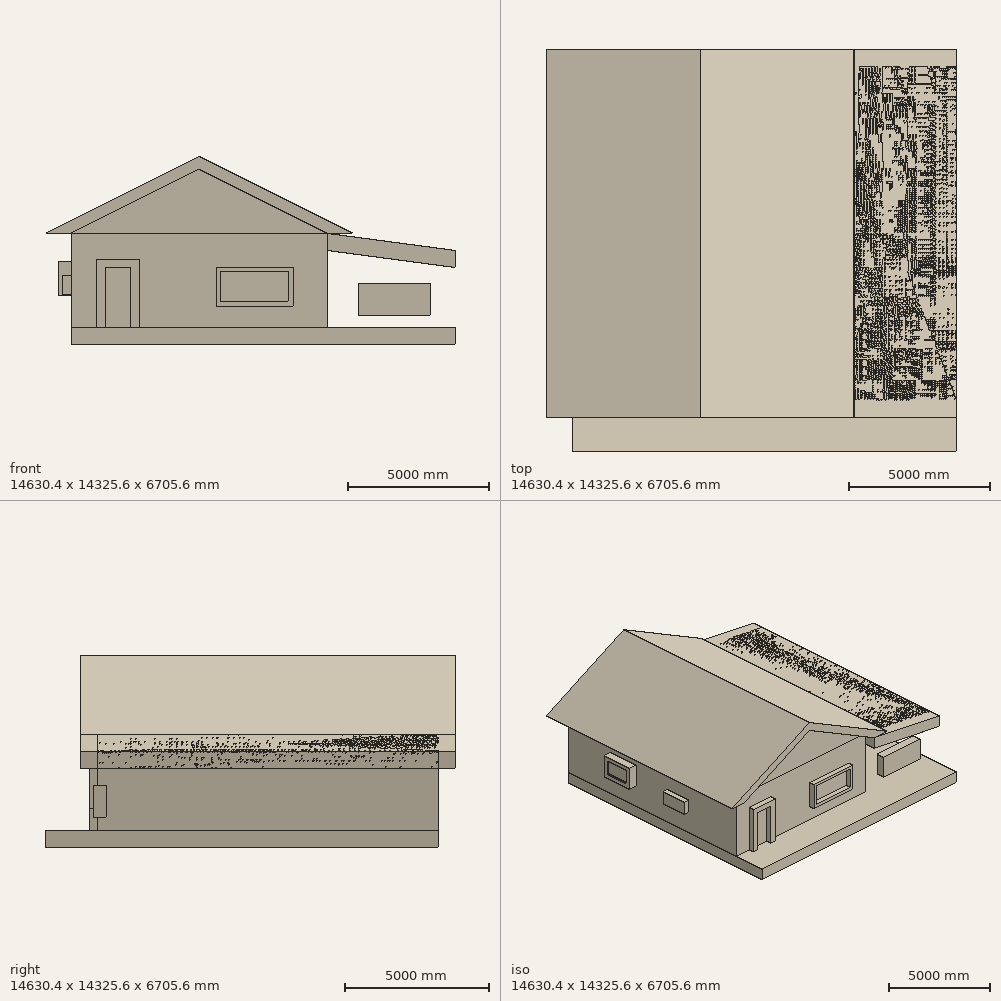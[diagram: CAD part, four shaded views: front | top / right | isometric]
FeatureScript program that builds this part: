
annotation { "Feature Type Name" : "Feature", "Feature Type Description" : "" }
export const myFeature = defineFeature(function(context is Context, id is Id, definition is map)
    precondition{}
    {
        {
            var Q0;
            Q0=qCreatedBy(makeId("Front.planeOp"),FACE);
            var sketch = newSketch(context, id + "F0", { "sketchPlane" : qUnion([Q0])});
            skLineSegment(sketch, "E0", {"start": v(0, 0) * mm, "end": v(-4572, 0) * mm});
            skLineSegment(sketch, "E1", {"start": v(0, 0) * mm, "end": v(4572, 0) * mm});
            skLineSegment(sketch, "E2", {"start": v(0, 0) * mm, "end": v(0, 2286) * mm});
            skLineSegment(sketch, "E3", {"start": v(-4572, 0) * mm, "end": v(-5486.4, 0) * mm});
            skLineSegment(sketch, "E4", {"start": v(4572, 0) * mm, "end": v(5486.4, 0) * mm});
            skLineSegment(sketch, "E5", {"start": v(0, 2286) * mm, "end": v(0, 2743.2) * mm});
            skLineSegment(sketch, "E6", {"start": v(-4572, 0) * mm, "end": v(0, 2286) * mm});
            skLineSegment(sketch, "E7", {"start": v(4572, 0) * mm, "end": v(0, 2286) * mm});
            skLineSegment(sketch, "E8", {"start": v(0, 2743.2) * mm, "end": v(5486.4, 0) * mm});
            skLineSegment(sketch, "E9", {"start": v(0, 2743.2) * mm, "end": v(-5486.4, 0) * mm});
            skLineSegment(sketch, "E10", {"start": v(-4572, 0) * mm, "end": v(-4572, -3352.8) * mm});
            skLineSegment(sketch, "E11", {"start": v(4572, 0) * mm, "end": v(4572, -3352.8) * mm});
            skLineSegment(sketch, "E12", {"start": v(4572, -3352.8) * mm, "end": v(4572, -3962.4) * mm});
            skLineSegment(sketch, "E13", {"start": v(-4572, -3352.8) * mm, "end": v(-4572, -3962.4) * mm});
            skLineSegment(sketch, "E14", {"start": v(-4572, -3352.8) * mm, "end": v(4572, -3352.8) * mm});
            skLineSegment(sketch, "E15", {"start": v(-4572, -3962.4) * mm, "end": v(4572, -3962.4) * mm});
            skLineSegment(sketch, "E16", {"start": v(4572, -3962.4) * mm, "end": v(9144, -3962.4) * mm});
            skLineSegment(sketch, "E17", {"start": v(4572, -3352.8) * mm, "end": v(9144, -3352.8) * mm});
            skLineSegment(sketch, "E18", {"start": v(9144, -3352.8) * mm, "end": v(9144, -3962.4) * mm});
            skLineSegment(sketch, "E19", {"start": v(9144, -3352.8) * mm, "end": v(9144, -609.6) * mm});
            skLineSegment(sketch, "E20", {"start": v(9144, -609.6) * mm, "end": v(4572, 0) * mm});
            skLineSegment(sketch, "E21", {"start": v(4572, 0) * mm, "end": v(4572, -609.6) * mm});
            skLineSegment(sketch, "E22", {"start": v(9144, -609.6) * mm, "end": v(9144, -1219.2) * mm});
            skLineSegment(sketch, "E23", {"start": v(4572, -609.6) * mm, "end": v(9144, -1219.2) * mm});
            skLineSegment(sketch, "E24", {"start": v(-3352.8, -3352.8) * mm, "end": v(-3352.8, -1219.2) * mm});
            skLineSegment(sketch, "E25", {"start": v(-3352.8, -1219.2) * mm, "end": v(-2438.4, -1219.2) * mm});
            skLineSegment(sketch, "E26", {"start": v(-2438.4, -3352.8) * mm, "end": v(-2438.4, -1219.2) * mm});
            skLineSegment(sketch, "E27.0", {"start": v(-3657.6, -3352.8) * mm, "end": v(-3657.6, -914.4) * mm});
            skLineSegment(sketch, "E27.1", {"start": v(-3657.6, -914.4) * mm, "end": v(-2133.6, -914.4) * mm});
            skLineSegment(sketch, "E27.2", {"start": v(-2133.6, -3352.8) * mm, "end": v(-2133.6, -914.4) * mm});
            skLineSegment(sketch, "E28.bottom", {"start": v(3352.8, -1219.2) * mm, "end": v(609.6, -1219.2) * mm});
            skLineSegment(sketch, "E28.top", {"start": v(609.6, -2590.8) * mm, "end": v(3352.8, -2590.8) * mm});
            skLineSegment(sketch, "E28.left", {"start": v(609.6, -2590.8) * mm, "end": v(609.6, -1219.2) * mm});
            skLineSegment(sketch, "E28.right", {"start": v(3352.8, -2590.8) * mm, "end": v(3352.8, -1219.2) * mm});
            skLineSegment(sketch, "E29.0", {"start": v(3200.4, -1371.6) * mm, "end": v(762, -1371.6) * mm});
            skLineSegment(sketch, "E29.1", {"start": v(3200.4, -2438.4) * mm, "end": v(3200.4, -1371.6) * mm});
            skLineSegment(sketch, "E29.2", {"start": v(762, -2438.4) * mm, "end": v(3200.4, -2438.4) * mm});
            skLineSegment(sketch, "E29.3", {"start": v(762, -2438.4) * mm, "end": v(762, -1371.6) * mm});
            skLineSegment(sketch, "E30.bottom", {"start": v(5683.3, -1784.2) * mm, "end": v(8242.86, -1784.2) * mm});
            skLineSegment(sketch, "E30.top", {"start": v(5683.3, -2924.87) * mm, "end": v(8242.86, -2924.87) * mm});
            skLineSegment(sketch, "E30.left", {"start": v(5683.3, -1784.2) * mm, "end": v(5683.3, -2924.87) * mm});
            skLineSegment(sketch, "E30.right", {"start": v(8242.86, -1784.2) * mm, "end": v(8242.86, -2924.87) * mm});
            skLineSegment(sketch, "E31.bottom", {"start": v(6044.98, -2173.7) * mm, "end": v(7909, -2173.7) * mm});
            skLineSegment(sketch, "E31.top", {"start": v(6044.98, -2591.02) * mm, "end": v(7909, -2591.02) * mm});
            skLineSegment(sketch, "E31.left", {"start": v(6044.98, -2173.7) * mm, "end": v(6044.98, -2591.02) * mm});
            skLineSegment(sketch, "E31.right", {"start": v(7909, -2173.7) * mm, "end": v(7909, -2591.02) * mm});
            skSolve(sketch);
        }
        {
            var Q0;
            Q0=makeQuery(id+"F0.imprint","IMPRINT",FACE,{"disambiguationData":[TD([[makeQuery(id+"F0.imprint","IMPRINT",EDGE,{"derivedFrom":sQuery(id+"F0.wireOp",EDGE,"E3")}),-1.0]])]});
            var Q1;
            Q1=makeQuery(id+"F0.imprint","IMPRINT",FACE,{"disambiguationData":[TD([[makeQuery(id+"F0.imprint","IMPRINT",EDGE,{"derivedFrom":sQuery(id+"F0.wireOp",EDGE,"E4")}),1.0]])]});
            var Q2;
            Q2=makeQuery(id+"F0.imprint","IMPRINT",FACE,{"disambiguationData":[TD([[makeQuery(id+"F0.imprint","IMPRINT",EDGE,{"derivedFrom":sQuery(id+"F0.wireOp",EDGE,"E20")}),1.0]])]});
            extrude(context, id + "F1", {"entities" : qUnion([Q0, Q1, Q2]), "depth" : 914.4 * mm, "offsetDistance" : 30.48 * mm, "hasSecondDirection" : true, "secondDirectionOppositeDirection" : true, "secondDirectionDepth" : 12192 * mm});
        }
        {
            var Q0;
            Q0=makeQuery(id+"F0.imprint","IMPRINT",FACE,{"disambiguationData":[TD([[makeQuery(id+"F0.imprint","IMPRINT",EDGE,{"derivedFrom":sQuery(id+"F0.wireOp",EDGE,"E0")}),-1.0]])]});
            var Q1;
            Q1=makeQuery(id+"F0.imprint","IMPRINT",FACE,{"disambiguationData":[TD([[makeQuery(id+"F0.imprint","IMPRINT",EDGE,{"derivedFrom":sQuery(id+"F0.wireOp",EDGE,"E1")}),1.0]])]});
            extrude(context, id + "F2", {"entities" : qUnion([Q0, Q1]), "operationType" : NewBodyOperationType.ADD, "depth" : 304.8 * mm, "offsetDistance" : 30.48 * mm, "hasSecondDirection" : true, "secondDirectionOppositeDirection" : true, "secondDirectionDepth" : 11582.4 * mm});
        }
        {
            var Q0;
            {var subQ4=sQuery(id+"F0.wireOp",EDGE,"E12");Q0=makeQuery(id+"F0.imprint","IMPRINT",FACE,{"disambiguationData":[TD([[makeQuery(id+"F0.imprint","IMPRINT",EDGE,{"derivedFrom":subQ4}),-1.0]])]});}
            var Q1;
            Q1=makeQuery(id+"F0.imprint","IMPRINT",FACE,{"disambiguationData":[TD([[makeQuery(id+"F0.imprint","IMPRINT",EDGE,{"derivedFrom":sQuery(id+"F0.wireOp",EDGE,"E12")}),1.0]])]});
            extrude(context, id + "F3", {"entities" : qUnion([Q0, Q1]), "depth" : 2133.6 * mm, "offsetDistance" : 30.48 * mm, "hasSecondDirection" : true, "secondDirectionOppositeDirection" : true, "secondDirectionDepth" : 11582.4 * mm});
        }
        {
            var Q0;
            Q0=makeQuery(id+"F0.imprint","IMPRINT",FACE,{"disambiguationData":[TD([[makeQuery(id+"F0.imprint","IMPRINT",EDGE,{"derivedFrom":sQuery(id+"F0.wireOp",EDGE,"E0")}),1.0]])]});
            var Q1;
            Q1=makeQuery(id+"F0.imprint","IMPRINT",FACE,{"disambiguationData":[TD([[makeQuery(id+"F0.imprint","IMPRINT",EDGE,{"derivedFrom":sQuery(id+"F0.wireOp",EDGE,"E11")}),1.0]])]});
            extrude(context, id + "F4", {"entities" : qUnion([Q0, Q1]), "depth" : 304.8 * mm, "offsetDistance" : 30.48 * mm, "hasSecondDirection" : true, "secondDirectionOppositeDirection" : true, "secondDirectionDepth" : 11582.4 * mm});
        }
        {
            var Q0;
            {var subQ0=sQuery(id+"F0.wireOp",EDGE,"E24");Q0=makeQuery(id+"F0.imprint","IMPRINT",FACE,{"disambiguationData":[TD([[makeQuery(id+"F0.imprint","IMPRINT",EDGE,{"derivedFrom":subQ0}),-1.0]])]});}
            var Q1;
            Q1=makeQuery(id+"F0.imprint","IMPRINT",FACE,{"disambiguationData":[TD([[makeQuery(id+"F0.imprint","IMPRINT",EDGE,{"derivedFrom":sQuery(id+"F0.wireOp",EDGE,"E29.0")}),1.0]])]});
            extrude(context, id + "F5", {"entities" : qUnion([Q0, Q1]), "operationType" : NewBodyOperationType.ADD, "depth" : 304.8 * mm, "offsetDistance" : 30.48 * mm});
        }
        {
            var Q0;
            Q0=makeQuery(id+"F0.imprint","IMPRINT",FACE,{"disambiguationData":[TD([[makeQuery(id+"F0.imprint","IMPRINT",EDGE,{"derivedFrom":sQuery(id+"F0.wireOp",EDGE,"E28.bottom")}),1.0]])]});
            var Q1;
            {var subQ0=sQuery(id+"F0.wireOp",EDGE,"E24");Q1=makeQuery(id+"F0.imprint","IMPRINT",FACE,{"disambiguationData":[TD([[makeQuery(id+"F0.imprint","IMPRINT",EDGE,{"derivedFrom":subQ0}),1.0]])]});}
            extrude(context, id + "F6", {"entities" : qUnion([Q0, Q1]), "depth" : 609.6 * mm, "offsetDistance" : 30.48 * mm});
        }
        {
            var Q0;
            Q0=makeQuery(id+"F4.opExtrude","SWEPT_FACE",FACE,{"disambiguationData":[OSD([sQuery(id+"F0.wireOp",EDGE,"E10")])]});
            var sketch = newSketch(context, id + "F7", { "sketchPlane" : qUnion([Q0])});
            skLineSegment(sketch, "E32.bottom", {"start": v(-8573.22, -995.9) * mm, "end": v(-6771.05, -995.9) * mm});
            skLineSegment(sketch, "E32.top", {"start": v(-8573.22, -2199.58) * mm, "end": v(-6771.05, -2199.58) * mm});
            skLineSegment(sketch, "E32.left", {"start": v(-8573.22, -995.9) * mm, "end": v(-8573.22, -2199.58) * mm});
            skLineSegment(sketch, "E32.right", {"start": v(-6771.05, -995.9) * mm, "end": v(-6771.05, -2199.58) * mm});
            skLineSegment(sketch, "E33.bottom", {"start": v(-4730.4, -1360.95) * mm, "end": v(-2764.48, -1360.95) * mm});
            skLineSegment(sketch, "E33.top", {"start": v(-4730.4, -2408.4) * mm, "end": v(-2764.48, -2408.4) * mm});
            skLineSegment(sketch, "E33.left", {"start": v(-4730.4, -1360.95) * mm, "end": v(-4730.4, -2408.4) * mm});
            skLineSegment(sketch, "E33.right", {"start": v(-2764.48, -1360.95) * mm, "end": v(-2764.48, -2408.4) * mm});
            skLineSegment(sketch, "E34.bottom", {"start": v(-8374.21, -1187.55) * mm, "end": v(-7019.55, -1187.55) * mm});
            skLineSegment(sketch, "E34.top", {"start": v(-8374.21, -1977.03) * mm, "end": v(-7019.55, -1977.03) * mm});
            skLineSegment(sketch, "E34.left", {"start": v(-8374.21, -1187.55) * mm, "end": v(-8374.21, -1977.03) * mm});
            skLineSegment(sketch, "E34.right", {"start": v(-7019.55, -1187.55) * mm, "end": v(-7019.55, -1977.03) * mm});
            skLineSegment(sketch, "E35.bottom", {"start": v(-4559.58, -1490.06) * mm, "end": v(-3043.05, -1490.06) * mm});
            skLineSegment(sketch, "E35.top", {"start": v(-4559.58, -2178.32) * mm, "end": v(-3043.05, -2178.32) * mm});
            skLineSegment(sketch, "E35.left", {"start": v(-4559.58, -1490.06) * mm, "end": v(-4559.58, -2178.32) * mm});
            skLineSegment(sketch, "E35.right", {"start": v(-3043.05, -1490.06) * mm, "end": v(-3043.05, -2178.32) * mm});
            skSolve(sketch);
        }
        {
            var Q0;
            Q0=makeQuery(id+"F7.imprint","IMPRINT",FACE,{"disambiguationData":[TD([[makeQuery(id+"F7.imprint","IMPRINT",EDGE,{"derivedFrom":sQuery(id+"F7.wireOp",EDGE,"E34.bottom")}),-1.0]])]});
            extrude(context, id + "F8", {"entities" : qUnion([Q0]), "operationType" : NewBodyOperationType.ADD, "depth" : 30.48 * mm, "offsetDistance" : 30.48 * mm});
        }
        {
            var Q0;
            Q0=makeQuery(id+"F7.imprint","IMPRINT",FACE,{"disambiguationData":[TD([[makeQuery(id+"F7.imprint","IMPRINT",EDGE,{"derivedFrom":sQuery(id+"F7.wireOp",EDGE,"E32.bottom")}),-1.0]])]});
            extrude(context, id + "F9", {"entities" : qUnion([Q0]), "operationType" : NewBodyOperationType.ADD, "depth" : 457.2 * mm, "offsetDistance" : 30.48 * mm});
        }
        {
            var Q0;
            Q0=makeQuery(id+"F8.opExtrude","CAP_FACE",FACE,{"disambiguationData":[OSD([sQuery(id+"F7.wireOp",EDGE,"E34.bottom"),sQuery(id+"F7.wireOp",EDGE,"E34.top"),sQuery(id+"F7.wireOp",EDGE,"E34.left"),sQuery(id+"F7.wireOp",EDGE,"E34.right")])],"isStart":false});
            extrude(context, id + "F10", {"entities" : qUnion([Q0]), "operationType" : NewBodyOperationType.ADD, "depth" : 304.8 * mm, "offsetDistance" : 30.48 * mm});
        }
        {
            var Q0;
            Q0=makeQuery(id+"F7.imprint","IMPRINT",FACE,{"disambiguationData":[TD([[makeQuery(id+"F7.imprint","IMPRINT",EDGE,{"derivedFrom":sQuery(id+"F7.wireOp",EDGE,"E35.bottom")}),-1.0]])]});
            extrude(context, id + "F11", {"entities" : qUnion([Q0]), "operationType" : NewBodyOperationType.ADD, "depth" : 304.8 * mm, "offsetDistance" : 30.48 * mm});
        }
        {
            var Q0;
            Q0=sQuery(id+"F7.wireOp",EDGE,"E33.top");
            var Q1;
            Q1=sQuery(id+"F7.wireOp",EDGE,"E33.left");
            var Q2;
            Q2=sQuery(id+"F7.wireOp",EDGE,"E33.bottom");
            var Q3;
            Q3=sQuery(id+"F7.wireOp",EDGE,"E33.right");
            extrude(context, id + "F12", {"bodyType" : ToolBodyType.SURFACE, "surfaceEntities" : qUnion([Q0, Q1, Q2, Q3]), "depth" : 457.2 * mm, "offsetDistance" : 30.48 * mm});
        }
        {
            var Q0;
            Q0=makeQuery(id+"F0.imprint","IMPRINT",FACE,{"disambiguationData":[TD([[makeQuery(id+"F0.imprint","IMPRINT",EDGE,{"derivedFrom":sQuery(id+"F0.wireOp",EDGE,"E30.bottom")}),-1.0]])]});
            var Q1;
            Q1=makeQuery(id+"F0.imprint","IMPRINT",FACE,{"disambiguationData":[TD([[makeQuery(id+"F0.imprint","IMPRINT",EDGE,{"derivedFrom":sQuery(id+"F0.wireOp",EDGE,"E31.bottom")}),-1.0]])]});
            extrude(context, id + "F13", {"entities" : qUnion([Q0, Q1]), "operationType" : NewBodyOperationType.ADD, "depth" : 457.2 * mm, "offsetDistance" : 30.48 * mm});
        }
        {
            var Q0;
            Q0=sQuery(id+"F0.wireOp",EDGE,"E31.bottom");
            var Q1;
            Q1=sQuery(id+"F0.wireOp",EDGE,"E31.top");
            extrude(context, id + "F14", {"bodyType" : ToolBodyType.SURFACE, "surfaceEntities" : qUnion([Q0, Q1]), "depth" : 304.8 * mm, "offsetDistance" : 30.48 * mm});
        }
        {
            var Q0;
            Q0=sQuery(id+"F0.wireOp",EDGE,"E31.bottom");
            var Q1;
            Q1=sQuery(id+"F0.wireOp",EDGE,"E31.top");
            extrude(context, id + "F15", {"bodyType" : ToolBodyType.SURFACE, "surfaceEntities" : qUnion([Q0, Q1]), "depth" : 304.8 * mm, "offsetDistance" : 30.48 * mm});
        }
    });
